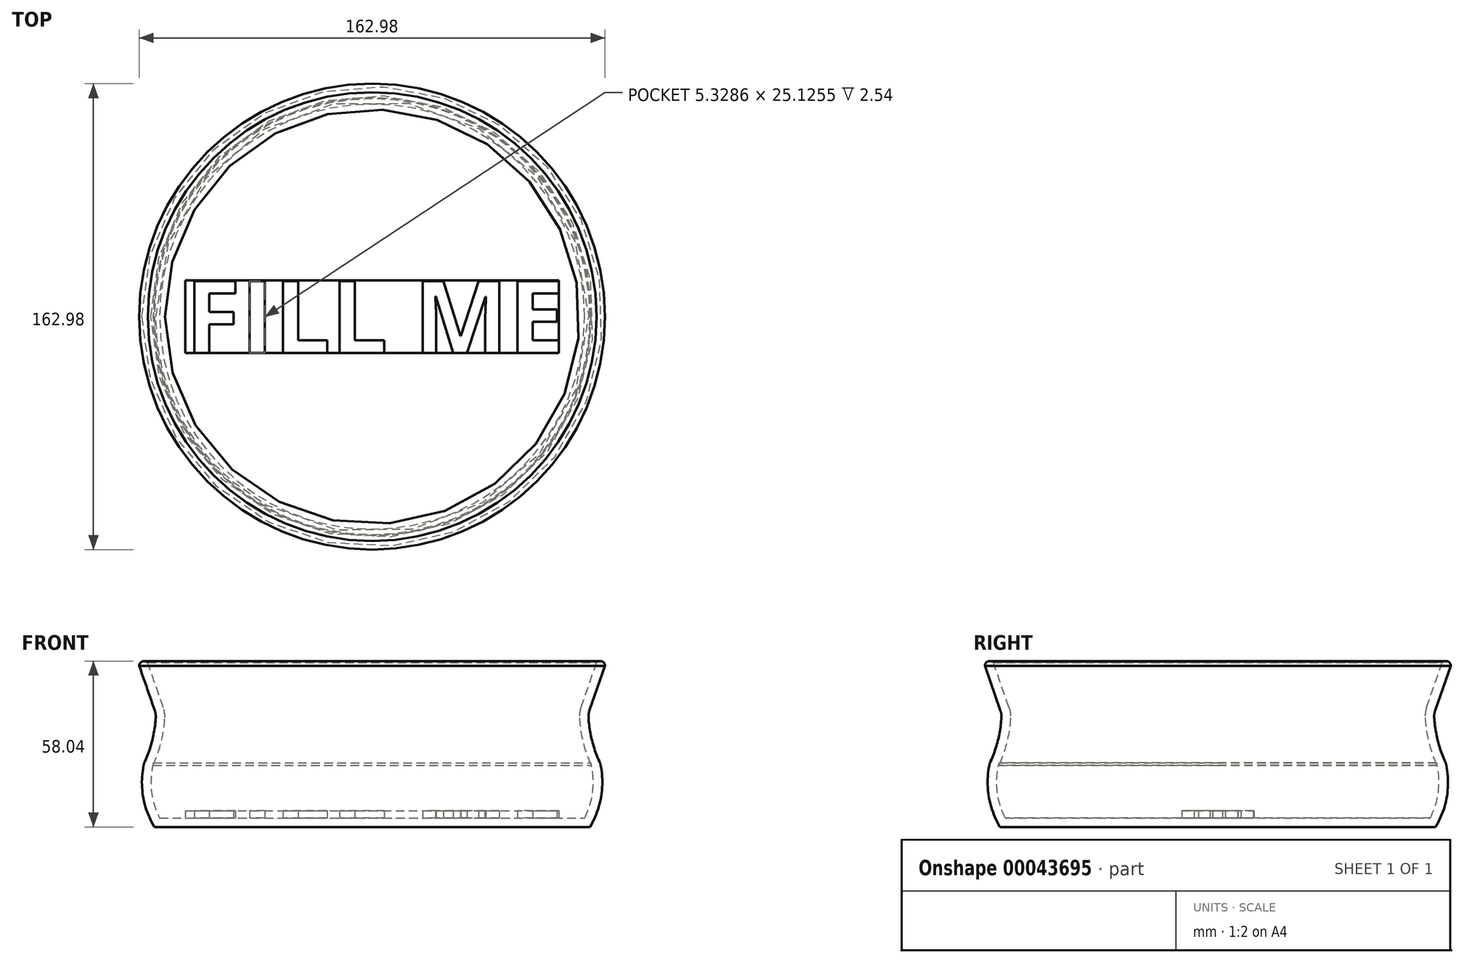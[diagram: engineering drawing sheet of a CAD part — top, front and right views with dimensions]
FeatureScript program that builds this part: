
annotation { "Feature Type Name" : "Feature", "Feature Type Description" : "" }
export const myFeature = defineFeature(function(context is Context, id is Id, definition is map)
    precondition{}
    {
        {
            var Q0;
            Q0=qCreatedBy(makeId("Front.planeOp"),FACE);
            var sketch = newSketch(context, id + "F0", { "sketchPlane" : qUnion([Q0])});
            skLineSegment(sketch, "E0", {"start": v(0, 0) * mm, "end": v(-76.2, 0) * mm});
            skArc(sketch, "E1", {"start": v(-79.97, 21.5) * mm, "mid": v(-80.09, 10.4) * mm, "end": v(-76.2, 0) * mm});
            skArc(sketch, "E2", {"start": v(-79.5, 22.93) * mm, "mid": v(-76.87, 30.45) * mm, "end": v(-75.7, 38.34) * mm});
            skLineSegment(sketch, "E3", {"start": v(-76.05, 40.75) * mm, "end": v(-81.5, 56.4) * mm});
            skPoint(sketch, "E4.visualSharp", {"position": v(-40.76, 41) * mm});
            skPoint(sketch, "E5.visualSharp", {"position": v(-75.66, 39.63) * mm});
            skArc(sketch, "E5.filletArc", {"start": v(-75.7, 38.34) * mm, "mid": v(-75.76, 39.56) * mm, "end": v(-76.05, 40.75) * mm});
            skPoint(sketch, "E6.visualSharp", {"position": v(-79.8, 22.3) * mm});
            skArc(sketch, "E6.filletArc", {"start": v(-79.5, 22.93) * mm, "mid": v(-79.78, 22.23) * mm, "end": v(-79.97, 21.5) * mm});
            skPoint(sketch, "E7.visualSharp", {"position": v(-45.27, 23.26) * mm});
            skArc(sketch, "E8.0", {"start": v(-76.5, 22.42) * mm, "mid": v(-77.2, 12.6) * mm, "end": v(-74.34, 3.17) * mm});
            skLineSegment(sketch, "E9", {"start": v(-74.34, 3.17) * mm, "end": v(0, 3.17) * mm});
            skLineSegment(sketch, "E10", {"start": v(0, 0) * mm, "end": v(0, 3.17) * mm});
            skArc(sketch, "E11.0", {"start": v(-76.62, 21.6) * mm, "mid": v(-73.79, 29.7) * mm, "end": v(-72.54, 38.18) * mm});
            skArc(sketch, "E12", {"start": v(-76.62, 21.6) * mm, "mid": v(-76.55, 22) * mm, "end": v(-76.5, 22.42) * mm});
            skLineSegment(sketch, "E13.0", {"start": v(-73.05, 41.8) * mm, "end": v(-78.5, 57.44) * mm});
            skArc(sketch, "E14", {"start": v(-72.54, 38.18) * mm, "mid": v(-72.62, 40.01) * mm, "end": v(-73.05, 41.8) * mm});
            skArc(sketch, "E15", {"start": v(-78.5, 57.44) * mm, "mid": v(-80.35, 57.95) * mm, "end": v(-81.5, 56.4) * mm});
            skSolve(sketch);
        }
        {
            var Q0;
            Q0=makeQuery(id+"F0.imprint","IMPRINT",FACE,{"disambiguationData":[TD([[makeQuery(id+"F0.imprint","IMPRINT",EDGE,{"derivedFrom":sQuery(id+"F0.wireOp",EDGE,"E0")}),-1.0]])]});
            var Q1;
            Q1=sQuery(id+"F0.wireOp",EDGE,"E10");
            revolve(context, id + "F1", {"entities" : qUnion([Q0]), "axis" : qUnion([Q1]), "revolveType" : RevolveType.FULL});
        }
        {
            var Q0;
            Q0=makeQuery(id+"F1.opRevolve","SWEPT_FACE",FACE,{"disambiguationData":[OSD([sQuery(id+"F0.wireOp",EDGE,"E9")])]});
            var sketch = newSketch(context, id + "F2", { "sketchPlane" : qUnion([Q0])});
            skLineSegment(sketch, "E16.rect.bottom", {"start": v(-65.36, 12.67) * mm, "end": v(65.36, 12.67) * mm});
            skLineSegment(sketch, "E16.rect.top", {"start": v(-65.36, -12.67) * mm, "end": v(65.36, -12.67) * mm});
            skLineSegment(sketch, "E16.rect.left", {"start": v(-65.36, 12.67) * mm, "end": v(-65.36, -12.67) * mm});
            skLineSegment(sketch, "E16.rect.right", {"start": v(65.36, 12.67) * mm, "end": v(65.36, -12.67) * mm});
            skPoint(sketch, "E16.rect.middle", {"position": v(0, 0) * mm});
            skText(sketch, "E17", { "text": "FILL ME", "fontName": "OpenSans-Bold.ttf"});
            const initialGuessF2  = {"E17": [-0.06536, -0.01267, 1, 0, 0.02534]};
            skSetInitialGuess(sketch, initialGuessF2);
            skSolve(sketch);
        }
        {
            var Q0;
            Q0 = qSketchRegion(id + "F2", true);
            extrude(context, id + "F3", {"entities" : qUnion([Q0]), "operationType" : NewBodyOperationType.ADD, "depth" : 2.54 * mm});
        }
    });
